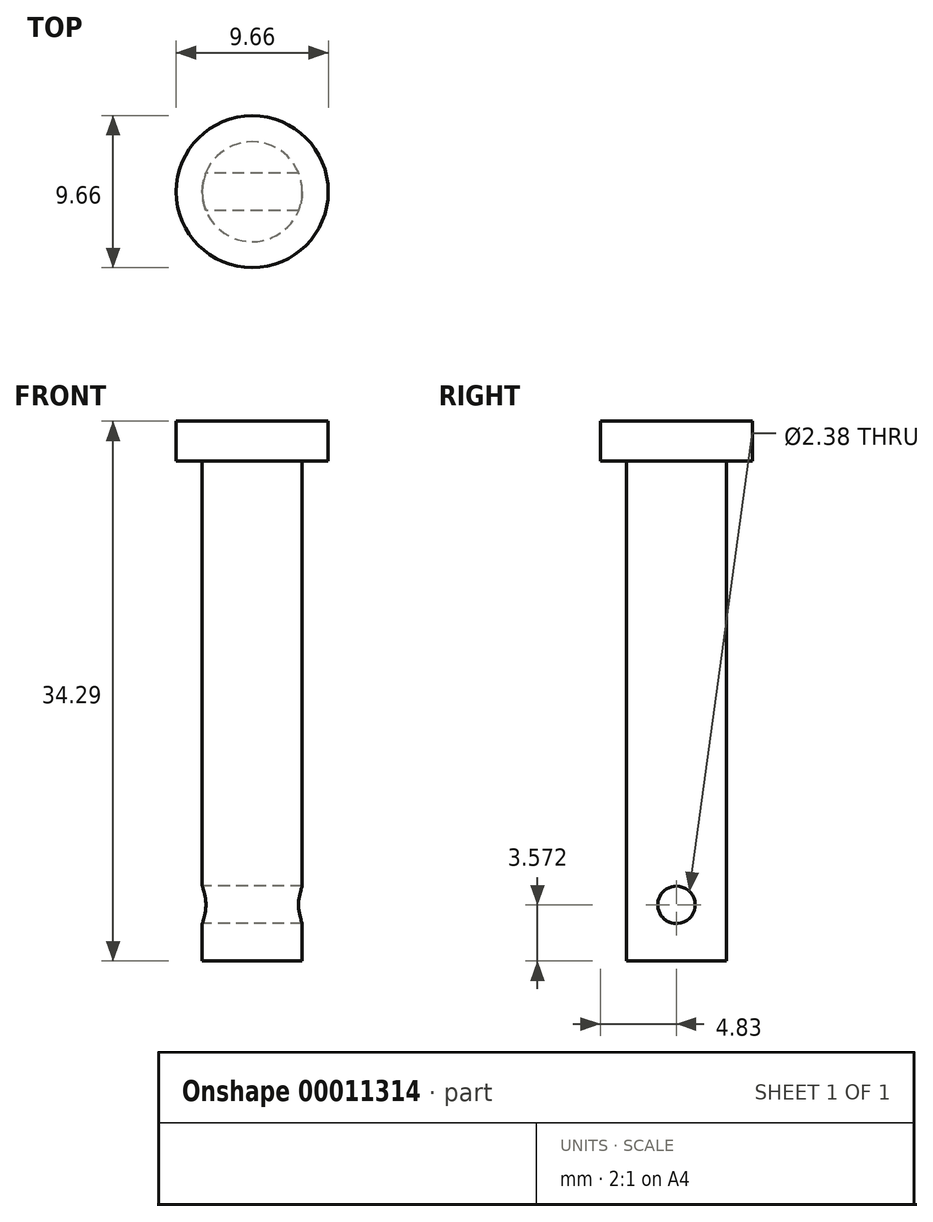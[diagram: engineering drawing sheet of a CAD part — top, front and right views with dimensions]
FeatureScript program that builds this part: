
annotation { "Feature Type Name" : "Feature", "Feature Type Description" : "" }
export const myFeature = defineFeature(function(context is Context, id is Id, definition is map)
    precondition{}
    {
        {
            var Q0;
            Q0=qCreatedBy(makeId("Top.planeOp"),FACE);
            var sketch = newSketch(context, id + "F0", { "sketchPlane" : qUnion([Q0])});
            skCircle(sketch, "E0", {"center": v(0, 0) * mm, "radius": 4.83 * mm});
            skCircle(sketch, "E1", {"center": v(0, 0) * mm, "radius": 3.18 * mm});
            skSolve(sketch);
        }
        {
            var Q0;
            Q0 = qSketchRegion(id + "F0", true);
            var Q1;
            Q1=makeQuery(id+"F0.imprint","IMPRINT",FACE,{"disambiguationData":[TD([[makeQuery(id+"F0.imprint","IMPRINT",EDGE,{"derivedFrom":sQuery(id+"F0.wireOp",EDGE,"E1")}),1.0]])]});
            extrude(context, id + "F1", {"entities" : qUnion([Q0, Q1]), "depth" : 2.54 * mm});
        }
        {
            var Q0;
            Q0=makeQuery(id+"F0.imprint","IMPRINT",FACE,{"disambiguationData":[TD([[makeQuery(id+"F0.imprint","IMPRINT",EDGE,{"derivedFrom":sQuery(id+"F0.wireOp",EDGE,"E1")}),1.0]])]});
            extrude(context, id + "F2", {"entities" : qUnion([Q0]), "operationType" : NewBodyOperationType.ADD, "oppositeDirection" : true, "depth" : 31.75 * mm});
        }
        {
            var Q0;
            Q0=qCreatedBy(makeId("Right.planeOp"),FACE);
            var sketch = newSketch(context, id + "F3", { "sketchPlane" : qUnion([Q0])});
            skCircle(sketch, "E2", {"center": v(0, -28.18) * mm, "radius": 1.2 * mm});
            skSolve(sketch);
        }
        {
            var Q0;
            Q0 = qSketchRegion(id + "F3", true);
            var Q1;
            Q1=makeQuery(id+"F2.opExtrude","SWEPT_FACE",FACE,{"disambiguationData":[OSD([sQuery(id+"F0.wireOp",EDGE,"E1")])]});
            var Q2;
            Q2=makeQuery(id+"F2.opExtrude","SWEPT_FACE",FACE,{"disambiguationData":[OSD([sQuery(id+"F0.wireOp",EDGE,"E1")])]});
            extrude(context, id + "F4", {"entities" : qUnion([Q0]), "operationType" : NewBodyOperationType.REMOVE, "endBound" : BoundingType.UP_TO_SURFACE, "endBoundEntityFace" : qUnion([Q1]), "depth" : 25.4 * mm, "hasSecondDirection" : true, "secondDirectionBound" : SecondDirectionBoundingType.UP_TO_SURFACE, "secondDirectionOppositeDirection" : true, "secondDirectionBoundEntityFace" : qUnion([Q2]), "secondDirectionDepth" : 25.4 * mm});
        }
    });
